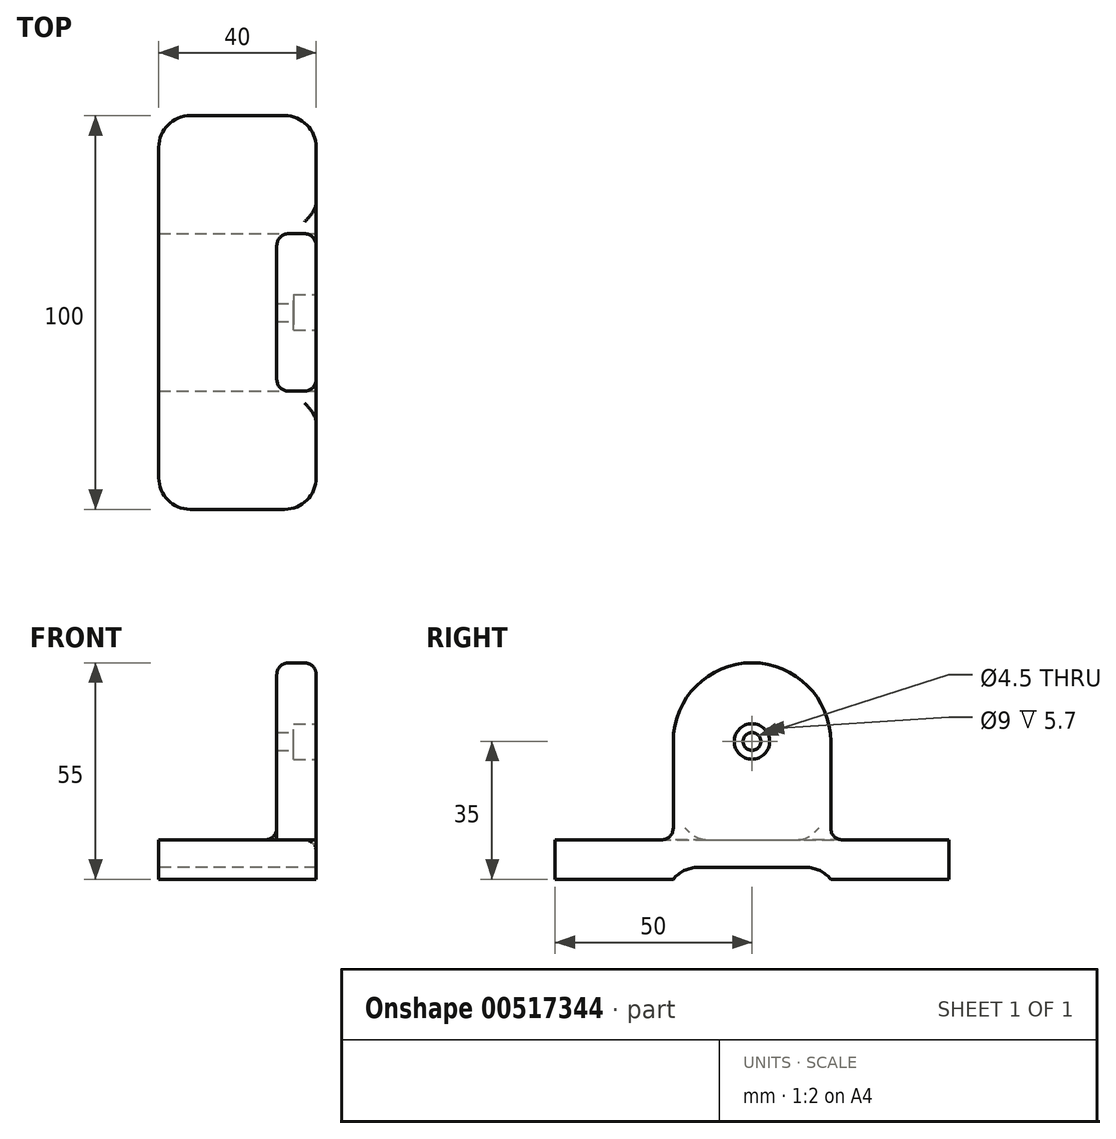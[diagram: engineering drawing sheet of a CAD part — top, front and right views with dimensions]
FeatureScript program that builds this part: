
annotation { "Feature Type Name" : "Feature", "Feature Type Description" : "" }
export const myFeature = defineFeature(function(context is Context, id is Id, definition is map)
    precondition{}
    {
        {
            var Q0;
            Q0=qCreatedBy(makeId("Top.planeOp"),FACE);
            var sketch = newSketch(context, id + "F0", { "sketchPlane" : qUnion([Q0])});
            skLineSegment(sketch, "E0.bottom", {"start": v(0, 0) * mm, "end": v(40, 0) * mm});
            skLineSegment(sketch, "E0.top", {"start": v(0, 100) * mm, "end": v(40, 100) * mm});
            skLineSegment(sketch, "E0.left", {"start": v(0, 0) * mm, "end": v(0, 100) * mm});
            skLineSegment(sketch, "E0.right", {"start": v(40, 0) * mm, "end": v(40, 100) * mm});
            skSolve(sketch);
        }
        {
            var Q0;
            Q0=makeQuery(id+"F0.imprint","IMPRINT",FACE,{"disambiguationData":[TD([[makeQuery(id+"F0.imprint","IMPRINT",EDGE,{"derivedFrom":sQuery(id+"F0.wireOp",EDGE,"E0.bottom")}),1.0]])]});
            extrude(context, id + "F1", {"entities" : qUnion([Q0]), "depth" : 10 * mm, "offsetDistance" : 25 * mm});
        }
        {
            var Q0;
            Q0=makeQuery(id+"F1.opExtrude","SWEPT_FACE",FACE,{"disambiguationData":[OSD([sQuery(id+"F0.wireOp",EDGE,"E0.right")])]});
            var sketch = newSketch(context, id + "F2", { "sketchPlane" : qUnion([Q0])});
            skLineSegment(sketch, "E1", {"start": v(30, 0) * mm, "end": v(30, 35) * mm});
            skArc(sketch, "E2", {"start": v(30, 35) * mm, "mid": v(50, 55) * mm, "end": v(70, 35) * mm});
            skLineSegment(sketch, "E3", {"start": v(70, 35) * mm, "end": v(70, 0) * mm});
            skLineSegment(sketch, "E4", {"start": v(30, 0) * mm, "end": v(70, 0) * mm});
            skSolve(sketch);
        }
        {
            var Q0;
            Q0 = qSketchRegion(id + "F2", true);
            extrude(context, id + "F3", {"entities" : qUnion([Q0]), "operationType" : NewBodyOperationType.ADD, "oppositeDirection" : true, "depth" : 10 * mm, "offsetDistance" : 25 * mm});
        }
        {
            var Q0;
            Q0=makeQuery(id+"F3.boolean.opBoolean","MERGE",FACE,{"derivedFrom":[makeQuery(id+"F1.opExtrude","SWEPT_FACE",FACE,{"disambiguationData":[OSD([sQuery(id+"F0.wireOp",EDGE,"E0.right")])]}),makeQuery(id+"F3.opExtrude","CAP_FACE",FACE,{"disambiguationData":[OSD([sQuery(id+"F2.wireOp",EDGE,"E1"),sQuery(id+"F2.wireOp",EDGE,"E2"),sQuery(id+"F2.wireOp",EDGE,"E3"),sQuery(id+"F2.wireOp",EDGE,"E4")])],"isStart":true})]});
            var sketch = newSketch(context, id + "F4", { "sketchPlane" : qUnion([Q0])});
            skLineSegment(sketch, "E5.bottom", {"start": v(30, 0) * mm, "end": v(70, 0) * mm});
            skLineSegment(sketch, "E5.top", {"start": v(30, 3) * mm, "end": v(70, 3) * mm});
            skLineSegment(sketch, "E5.left", {"start": v(30, 0) * mm, "end": v(30, 3) * mm});
            skLineSegment(sketch, "E5.right", {"start": v(70, 0) * mm, "end": v(70, 3) * mm});
            skSolve(sketch);
        }
        {
            var Q0;
            Q0 = qSketchRegion(id + "F4", true);
            extrude(context, id + "F5", {"entities" : qUnion([Q0]), "operationType" : NewBodyOperationType.REMOVE, "endBound" : BoundingType.THROUGH_ALL, "oppositeDirection" : true, "depth" : 25 * mm, "offsetDistance" : 25 * mm});
        }
        {
            var Q0;
            Q0=makeQuery(id+"F3.boolean.opBoolean","MERGE",FACE,{"derivedFrom":[makeQuery(id+"F1.opExtrude","SWEPT_FACE",FACE,{"disambiguationData":[OSD([sQuery(id+"F0.wireOp",EDGE,"E0.right")])]}),makeQuery(id+"F3.opExtrude","CAP_FACE",FACE,{"disambiguationData":[OSD([sQuery(id+"F2.wireOp",EDGE,"E1"),sQuery(id+"F2.wireOp",EDGE,"E2"),sQuery(id+"F2.wireOp",EDGE,"E3"),sQuery(id+"F2.wireOp",EDGE,"E4")])],"isStart":true})]});
            var sketch = newSketch(context, id + "F6", { "sketchPlane" : qUnion([Q0])});
            skCircle(sketch, "E6", {"center": v(50, 35) * mm, "radius": 2.25 * mm});
            skSolve(sketch);
        }
        {
            var Q0;
            Q0 = qSketchRegion(id + "F6", true);
            extrude(context, id + "F7", {"entities" : qUnion([Q0]), "operationType" : NewBodyOperationType.REMOVE, "endBound" : BoundingType.THROUGH_ALL, "oppositeDirection" : true, "depth" : 25 * mm, "offsetDistance" : 25 * mm});
        }
        {
            var Q0;
            Q0=makeQuery(id+"F3.boolean.opBoolean","MERGE",FACE,{"derivedFrom":[makeQuery(id+"F1.opExtrude","SWEPT_FACE",FACE,{"disambiguationData":[OSD([sQuery(id+"F0.wireOp",EDGE,"E0.right")])]}),makeQuery(id+"F3.opExtrude","CAP_FACE",FACE,{"disambiguationData":[OSD([sQuery(id+"F2.wireOp",EDGE,"E1"),sQuery(id+"F2.wireOp",EDGE,"E2"),sQuery(id+"F2.wireOp",EDGE,"E3"),sQuery(id+"F2.wireOp",EDGE,"E4")])],"isStart":true})]});
            var sketch = newSketch(context, id + "F8", { "sketchPlane" : qUnion([Q0])});
            skCircle(sketch, "E7", {"center": v(50, 35) * mm, "radius": 4.5 * mm});
            skSolve(sketch);
        }
        {
            var Q0;
            Q0 = qSketchRegion(id + "F8", true);
            extrude(context, id + "F9", {"entities" : qUnion([Q0]), "operationType" : NewBodyOperationType.REMOVE, "oppositeDirection" : true, "depth" : 5.7 * mm, "offsetDistance" : 25 * mm});
        }
        {
            var Q0;
            Q0=makeQuery(id+"F1.opExtrude","SWEPT_EDGE",EDGE,{"disambiguationData":[OSD([sQuery(id+"F0.wireOp",EDGE,"E0.bottom"),sQuery(id+"F0.wireOp",EDGE,"E0.right")])]});
            var Q1;
            Q1=makeQuery(id+"F1.opExtrude","SWEPT_EDGE",EDGE,{"disambiguationData":[OSD([sQuery(id+"F0.wireOp",EDGE,"E0.bottom"),sQuery(id+"F0.wireOp",EDGE,"E0.left")])]});
            var Q2;
            Q2=makeQuery(id+"F1.opExtrude","SWEPT_EDGE",EDGE,{"disambiguationData":[OSD([sQuery(id+"F0.wireOp",EDGE,"E0.top"),sQuery(id+"F0.wireOp",EDGE,"E0.left")])]});
            var Q3;
            Q3=makeQuery(id+"F1.opExtrude","SWEPT_EDGE",EDGE,{"disambiguationData":[OSD([sQuery(id+"F0.wireOp",EDGE,"E0.top"),sQuery(id+"F0.wireOp",EDGE,"E0.right")])]});
            var Q4;
            Q4=makeQuery(id+"F5.boolean.opBoolean","COPY",EDGE,{"derivedFrom":makeQuery(id+"F5.opExtrude","SWEPT_EDGE",EDGE,{"disambiguationData":[OSD([sQuery(id+"F4.wireOp",EDGE,"E5.top"),sQuery(id+"F4.wireOp",EDGE,"E5.left")])]})});
            var Q5;
            Q5=makeQuery(id+"F5.boolean.opBoolean","COPY",EDGE,{"derivedFrom":makeQuery(id+"F5.opExtrude","SWEPT_EDGE",EDGE,{"disambiguationData":[OSD([sQuery(id+"F4.wireOp",EDGE,"E5.top"),sQuery(id+"F4.wireOp",EDGE,"E5.right")])]})});
            fillet(context, id + "F10", {"entities" : qUnion([Q0, Q1, Q2, Q3, Q4, Q5]), "radius" : 8 * mm, "tangentPropagation" : true, "allowEdgeOverflow" : false});
        }
        {
            var Q0;
            Q0=makeQuery(id+"F3.opExtrude","CAP_EDGE",EDGE,{"disambiguationData":[OSD([sQuery(id+"F2.wireOp",EDGE,"E2")])],"isStart":true});
            var Q1;
            Q1=makeQuery(id+"F3.opExtrude","CAP_EDGE",EDGE,{"disambiguationData":[OSD([sQuery(id+"F2.wireOp",EDGE,"E2")])],"isStart":false});
            var Q2;
            Q2=makeQuery(id+"F3.boolean.opBoolean","INTERSECT",EDGE,{"derivedFrom":[makeQuery(id+"F1.opExtrude","CAP_FACE",FACE,{"disambiguationData":[OSD([sQuery(id+"F0.wireOp",EDGE,"E0.bottom"),sQuery(id+"F0.wireOp",EDGE,"E0.top"),sQuery(id+"F0.wireOp",EDGE,"E0.left"),sQuery(id+"F0.wireOp",EDGE,"E0.right")])],"isStart":false}),makeQuery(id+"F3.opExtrude","SWEPT_FACE",FACE,{"disambiguationData":[OSD([sQuery(id+"F2.wireOp",EDGE,"E3")])]})]});
            var Q3;
            Q3=makeQuery(id+"F3.boolean.opBoolean","INTERSECT",EDGE,{"derivedFrom":[makeQuery(id+"F1.opExtrude","CAP_FACE",FACE,{"disambiguationData":[OSD([sQuery(id+"F0.wireOp",EDGE,"E0.bottom"),sQuery(id+"F0.wireOp",EDGE,"E0.top"),sQuery(id+"F0.wireOp",EDGE,"E0.left"),sQuery(id+"F0.wireOp",EDGE,"E0.right")])],"isStart":false}),makeQuery(id+"F3.opExtrude","SWEPT_FACE",FACE,{"disambiguationData":[OSD([sQuery(id+"F2.wireOp",EDGE,"E1")])]})]});
            fillet(context, id + "F11", {"entities" : qUnion([Q0, Q1, Q2, Q3]), "radius" : 3 * mm, "tangentPropagation" : true, "allowEdgeOverflow" : false});
        }
    });
